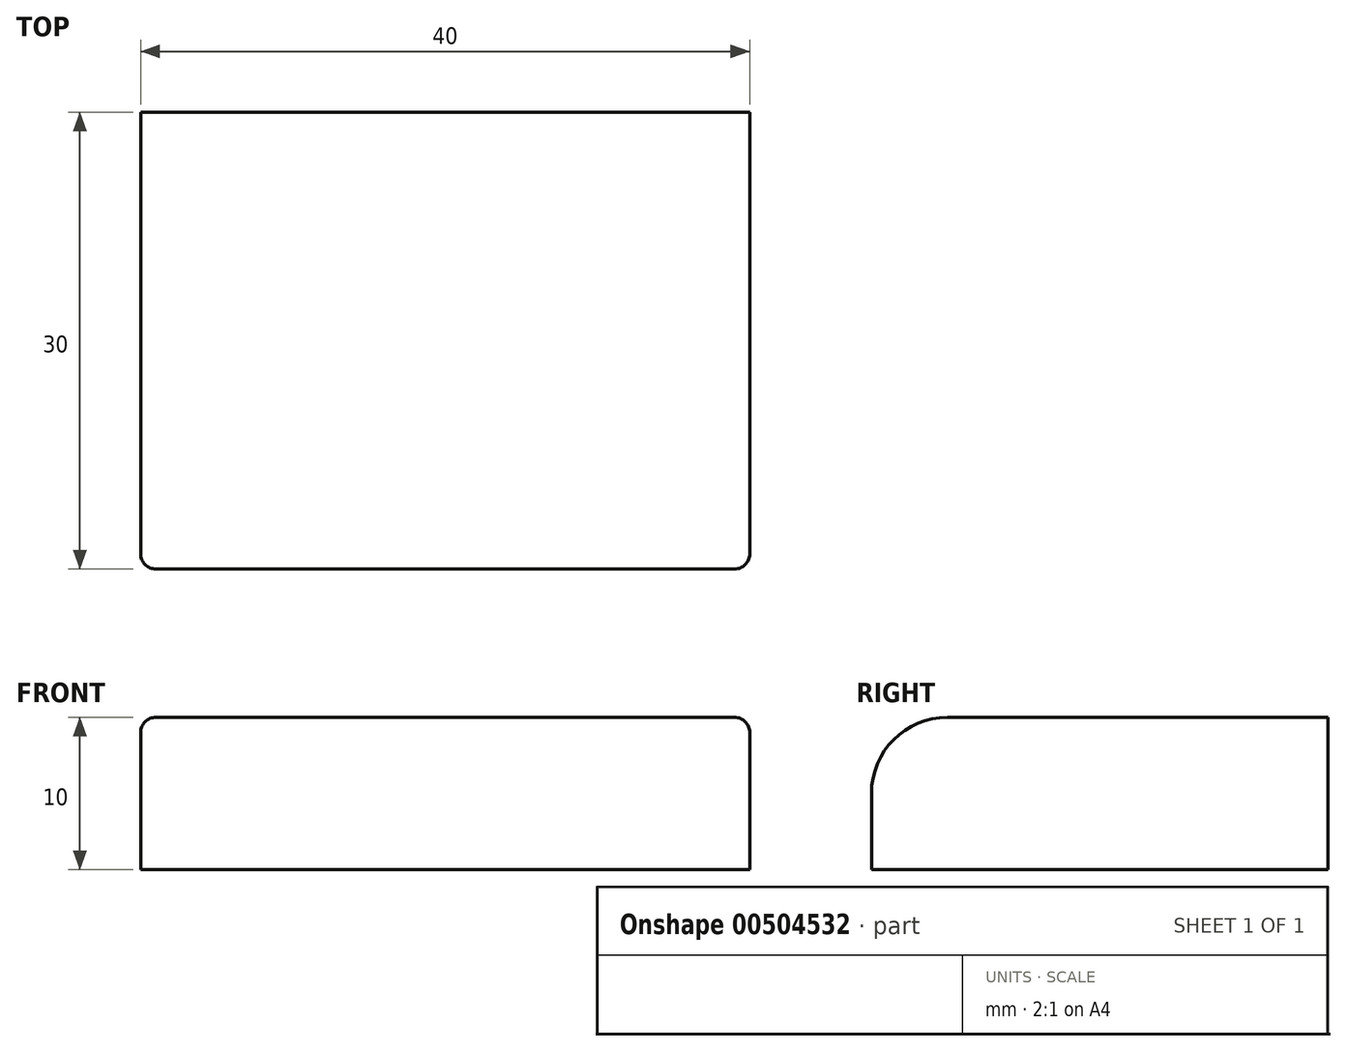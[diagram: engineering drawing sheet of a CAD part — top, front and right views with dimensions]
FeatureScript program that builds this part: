
annotation { "Feature Type Name" : "Feature", "Feature Type Description" : "" }
export const myFeature = defineFeature(function(context is Context, id is Id, definition is map)
    precondition{}
    {
        {
            var Q0;
            Q0=qCreatedBy(makeId("Right.planeOp"),FACE);
            var sketch = newSketch(context, id + "F0", { "sketchPlane" : qUnion([Q0])});
            skLineSegment(sketch, "E0.bottom", {"start": v(-15.2, 0) * mm, "end": v(14.8, 0) * mm});
            skLineSegment(sketch, "E0.top", {"start": v(-10.2, 10) * mm, "end": v(14.8, 10) * mm});
            skLineSegment(sketch, "E0.left", {"start": v(-15.2, 0) * mm, "end": v(-15.2, 5) * mm});
            skLineSegment(sketch, "E0.right", {"start": v(14.8, 0) * mm, "end": v(14.8, 10) * mm});
            skPoint(sketch, "E1.visualSharp", {"position": v(-15.2, 10) * mm});
            skArc(sketch, "E1.filletArc", {"start": v(-10.2, 10) * mm, "mid": v(-13.73, 8.54) * mm, "end": v(-15.2, 5) * mm});
            skSolve(sketch);
        }
        {
            var Q0;
            Q0=makeQuery(id+"F0.imprint","IMPRINT",FACE,{"disambiguationData":[TD([[makeQuery(id+"F0.imprint","IMPRINT",EDGE,{"derivedFrom":sQuery(id+"F0.wireOp",EDGE,"E0.bottom")}),1.0]])]});
            extrude(context, id + "F1", {"entities" : qUnion([Q0]), "depth" : 40 * mm, "offsetDistance" : 25 * mm});
        }
        {
            var Q0;
            Q0=makeQuery(id+"F1.opExtrude","CAP_EDGE",EDGE,{"disambiguationData":[OSD([sQuery(id+"F0.wireOp",EDGE,"E0.top")])],"isStart":false});
            fillet(context, id + "F2", {"entities" : qUnion([Q0]), "radius" : 1 * mm, "tangentPropagation" : true, "allowEdgeOverflow" : false});
        }
        {
            var Q0;
            Q0=makeQuery(id+"F1.opExtrude","CAP_EDGE",EDGE,{"disambiguationData":[OSD([sQuery(id+"F0.wireOp",EDGE,"E0.top")])],"isStart":true});
            fillet(context, id + "F3", {"entities" : qUnion([Q0]), "radius" : 1 * mm, "tangentPropagation" : true, "allowEdgeOverflow" : false});
        }
    });
